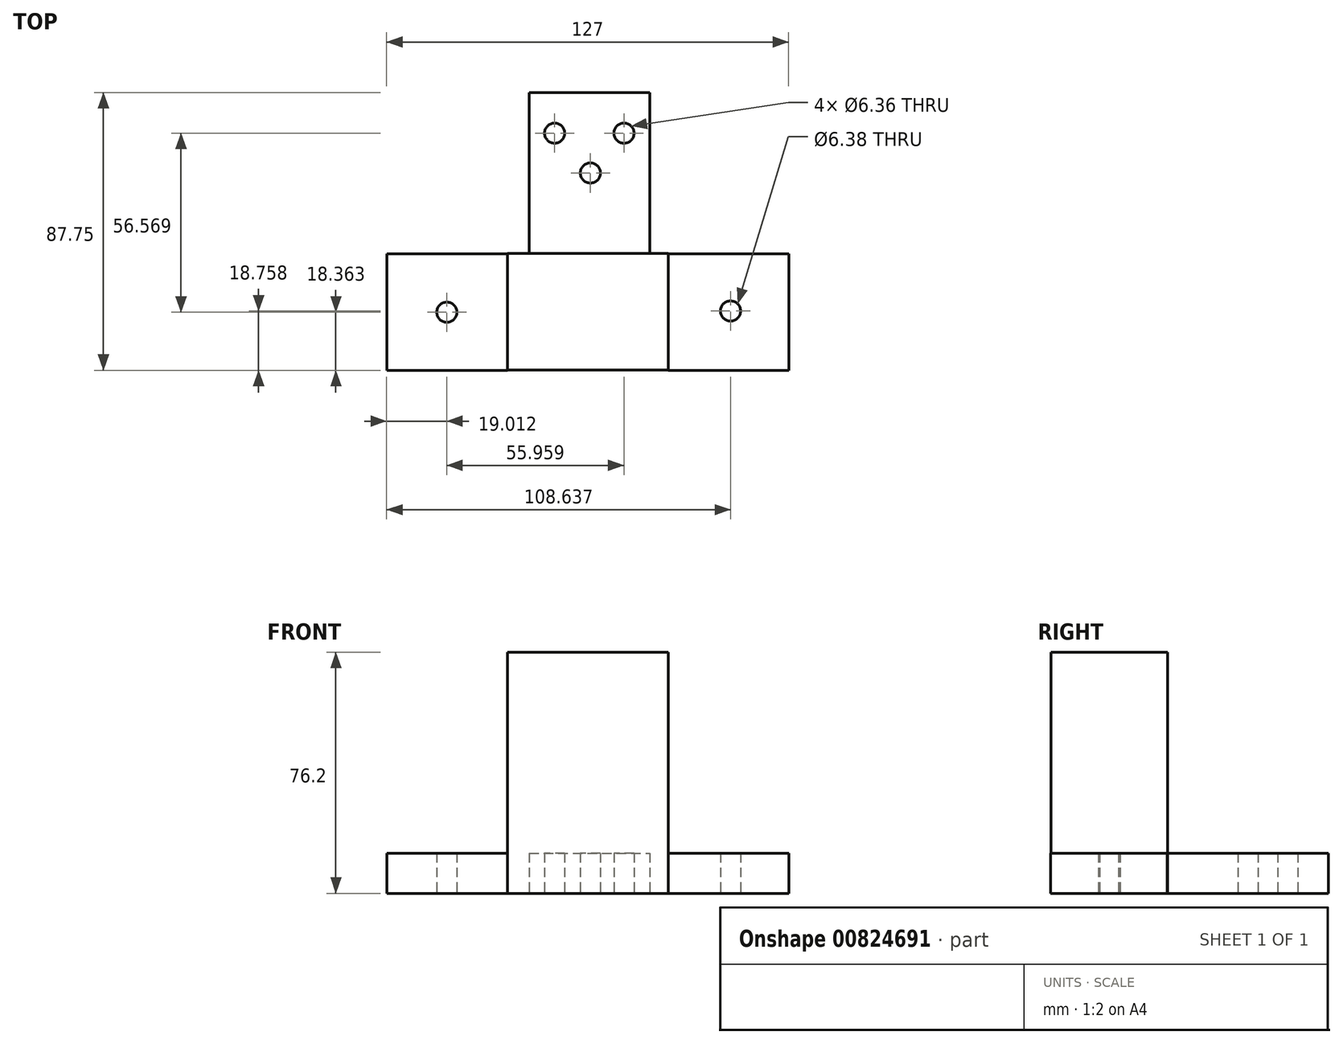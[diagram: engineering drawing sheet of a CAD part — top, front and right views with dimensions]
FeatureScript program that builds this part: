
annotation { "Feature Type Name" : "Feature", "Feature Type Description" : "" }
export const myFeature = defineFeature(function(context is Context, id is Id, definition is map)
    precondition{}
    {
        {
            var Q0;
            Q0=qCreatedBy(makeId("Top.planeOp"),FACE);
            var sketch = newSketch(context, id + "F0", { "sketchPlane" : qUnion([Q0])});
            skLineSegment(sketch, "E0.bottom", {"start": v(-70.89, 7.03) * mm, "end": v(-20.09, 7.03) * mm});
            skLineSegment(sketch, "E0.top", {"start": v(-70.89, -29.8) * mm, "end": v(-20.09, -29.8) * mm});
            skLineSegment(sketch, "E0.left", {"start": v(-70.89, 7.03) * mm, "end": v(-70.89, -29.8) * mm});
            skLineSegment(sketch, "E0.right", {"start": v(-20.09, 7.03) * mm, "end": v(-20.09, -29.8) * mm});
            skLineSegment(sketch, "E1.bottom", {"start": v(-108.99, 6.9) * mm, "end": v(-70.89, 6.9) * mm});
            skLineSegment(sketch, "E1.top", {"start": v(-108.99, -29.92) * mm, "end": v(-70.89, -29.92) * mm});
            skLineSegment(sketch, "E1.left", {"start": v(-108.99, 6.9) * mm, "end": v(-108.99, -29.92) * mm});
            skLineSegment(sketch, "E1.right", {"start": v(-70.89, 6.9) * mm, "end": v(-70.89, -29.92) * mm});
            skLineSegment(sketch, "E2.bottom", {"start": v(-20.09, 6.9) * mm, "end": v(18.01, 6.9) * mm});
            skLineSegment(sketch, "E2.top", {"start": v(-20.09, -29.92) * mm, "end": v(18.01, -29.92) * mm});
            skLineSegment(sketch, "E2.left", {"start": v(-20.09, 6.9) * mm, "end": v(-20.09, -29.92) * mm});
            skLineSegment(sketch, "E2.right", {"start": v(18.01, 6.9) * mm, "end": v(18.01, -29.92) * mm});
            skCircle(sketch, "E3", {"center": v(-89.98, -11.56) * mm, "radius": 3.18 * mm});
            skCircle(sketch, "E4", {"center": v(-0.35, -11.16) * mm, "radius": 3.2 * mm});
            skLineSegment(sketch, "E5.bottom", {"start": v(-63.96, 7.03) * mm, "end": v(-25.86, 7.03) * mm});
            skLineSegment(sketch, "E5.top", {"start": v(-63.96, 57.83) * mm, "end": v(-25.86, 57.83) * mm});
            skLineSegment(sketch, "E5.left", {"start": v(-63.96, 7.03) * mm, "end": v(-63.96, 57.83) * mm});
            skLineSegment(sketch, "E5.right", {"start": v(-25.86, 7.03) * mm, "end": v(-25.86, 57.83) * mm});
            skCircle(sketch, "E6", {"center": v(-44.61, 32.43) * mm, "radius": 3.18 * mm});
            skPoint(sketch, "E7", {"position": v(-63.96, 32.43) * mm});
            skCircle(sketch, "E8", {"center": v(-55.91, 45.01) * mm, "radius": 3.18 * mm});
            skCircle(sketch, "E9", {"center": v(-34.02, 45.01) * mm, "radius": 3.18 * mm});
            skSolve(sketch);
        }
        {
            var Q0;
            {var subQ0=sQuery(id+"F0.wireOp",EDGE,"E0.top");Q0=makeQuery(id+"F0.imprint","IMPRINT",FACE,{"disambiguationData":[TD([[makeQuery(id+"F0.imprint","IMPRINT",EDGE,{"derivedFrom":subQ0}),1.0]])]});}
            extrude(context, id + "F1", {"entities" : qUnion([Q0]), "depth" : 76.2 * mm, "offsetDistance" : 25.4 * mm});
        }
        {
            var Q0;
            {var subQ0=sQuery(id+"F0.wireOp",EDGE,"E1.bottom");Q0=makeQuery(id+"F0.imprint","IMPRINT",FACE,{"disambiguationData":[TD([[makeQuery(id+"F0.imprint","IMPRINT",EDGE,{"derivedFrom":subQ0}),-1.0]])]});}
            extrude(context, id + "F2", {"entities" : qUnion([Q0]), "operationType" : NewBodyOperationType.ADD, "depth" : 12.7 * mm, "offsetDistance" : 25.4 * mm});
        }
        {
            var Q0;
            {var subQ1=sQuery(id+"F0.wireOp",EDGE,"E2.bottom");Q0=makeQuery(id+"F0.imprint","IMPRINT",FACE,{"disambiguationData":[TD([[makeQuery(id+"F0.imprint","IMPRINT",EDGE,{"derivedFrom":subQ1}),-1.0]])]});}
            extrude(context, id + "F3", {"entities" : qUnion([Q0]), "operationType" : NewBodyOperationType.ADD, "depth" : 12.7 * mm, "offsetDistance" : 25.4 * mm});
        }
        {
            var Q0;
            Q0=makeQuery(id+"F0.imprint","IMPRINT",FACE,{"disambiguationData":[TD([[makeQuery(id+"F0.imprint","IMPRINT",EDGE,{"derivedFrom":sQuery(id+"F0.wireOp",EDGE,"E5.top")}),-1.0]])]});
            extrude(context, id + "F4", {"entities" : qUnion([Q0]), "operationType" : NewBodyOperationType.ADD, "depth" : 12.7 * mm, "offsetDistance" : 25.4 * mm});
        }
    });
